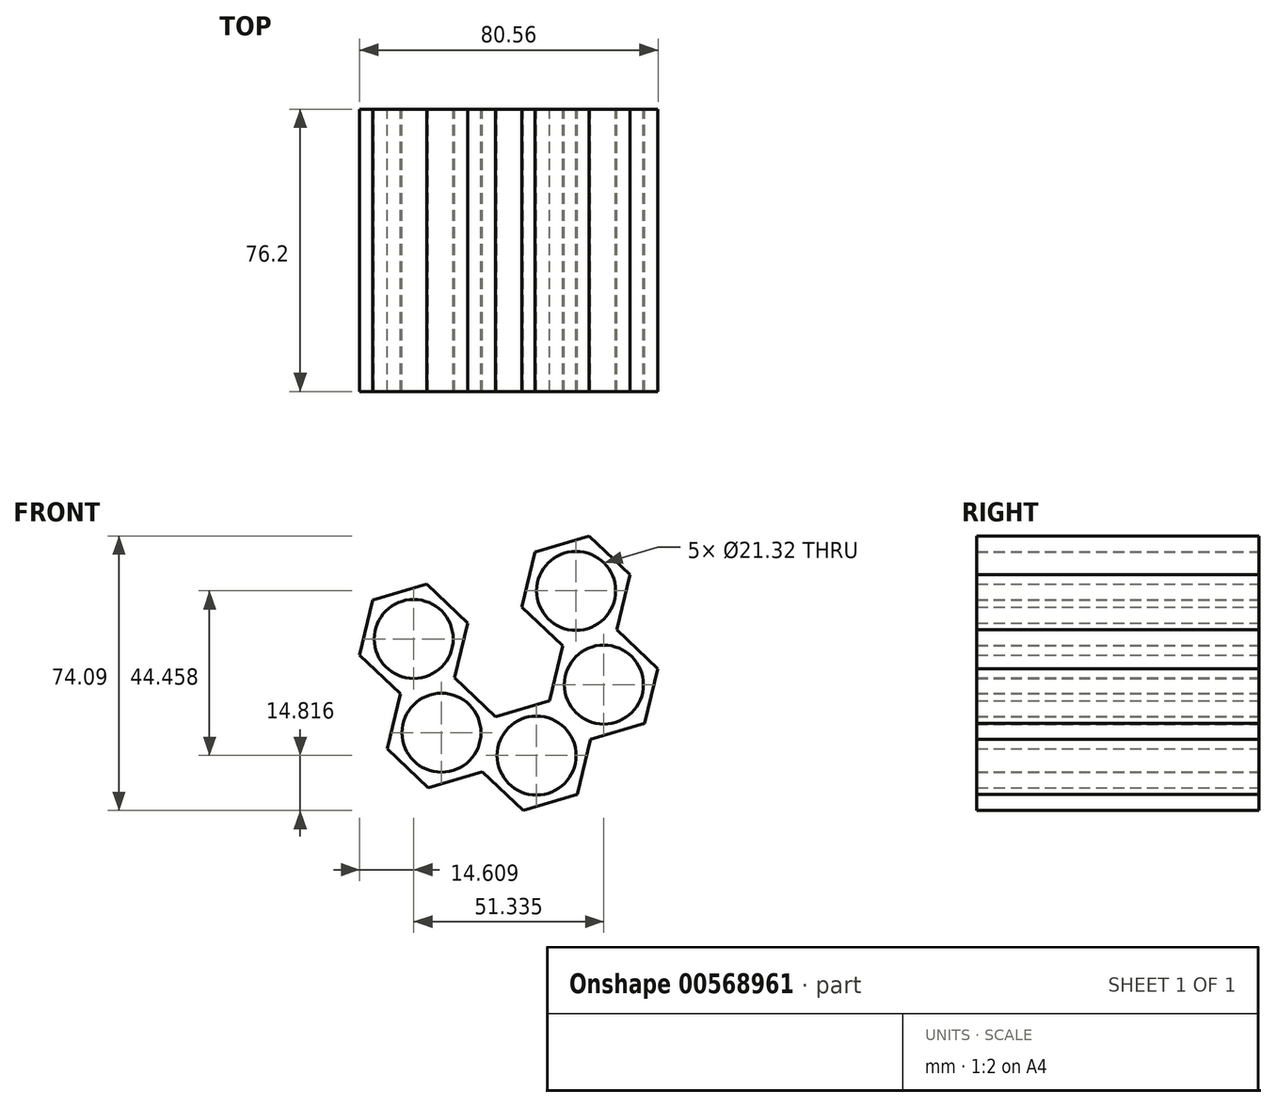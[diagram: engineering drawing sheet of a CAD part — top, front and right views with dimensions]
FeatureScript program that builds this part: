
annotation { "Feature Type Name" : "Feature", "Feature Type Description" : "" }
export const myFeature = defineFeature(function(context is Context, id is Id, definition is map)
    precondition{}
    {
        {
            var Q0;
            Q0=qCreatedBy(makeId("Front.planeOp"),FACE);
            var sketch = newSketch(context, id + "F0", { "sketchPlane" : qUnion([Q0])});
            skCircle(sketch, "E0.cCircle", {"center": v(-51.5, 29.02) * mm, "radius": 13.2 * mm, "construction": true});
            skLineSegment(sketch, "E0.0", {"start": v(-36.89, 33.35) * mm, "end": v(-40.45, 18.53) * mm});
            skLineSegment(sketch, "E0.1", {"start": v(-40.45, 18.53) * mm, "end": v(-55.06, 14.2) * mm});
            skLineSegment(sketch, "E0.2", {"start": v(-55.06, 14.2) * mm, "end": v(-66.11, 24.7) * mm});
            skLineSegment(sketch, "E0.3", {"start": v(-66.11, 24.7) * mm, "end": v(-62.56, 39.51) * mm});
            skLineSegment(sketch, "E0.4", {"start": v(-62.56, 39.51) * mm, "end": v(-47.94, 43.84) * mm});
            skLineSegment(sketch, "E0.5", {"start": v(-47.94, 43.84) * mm, "end": v(-36.89, 33.35) * mm});
            skPoint(sketch, "E0.0.midPoint", {"position": v(-38.67, 25.94) * mm});
            skCircle(sketch, "E1.cCircle", {"center": v(-25.83, 22.86) * mm, "radius": 13.2 * mm, "construction": true});
            skLineSegment(sketch, "E1.0", {"start": v(-11.22, 27.2) * mm, "end": v(-14.78, 12.37) * mm});
            skLineSegment(sketch, "E1.1", {"start": v(-14.78, 12.37) * mm, "end": v(-29.4, 8.05) * mm});
            skLineSegment(sketch, "E1.2", {"start": v(-29.4, 8.05) * mm, "end": v(-40.45, 18.53) * mm});
            skLineSegment(sketch, "E1.3", {"start": v(-40.45, 18.53) * mm, "end": v(-36.89, 33.35) * mm});
            skLineSegment(sketch, "E1.4", {"start": v(-36.89, 33.35) * mm, "end": v(-22.28, 37.68) * mm});
            skLineSegment(sketch, "E1.5", {"start": v(-22.28, 37.68) * mm, "end": v(-11.22, 27.2) * mm});
            skPoint(sketch, "E1.0.midPoint", {"position": v(-13, 19.78) * mm});
            skCircle(sketch, "E2.cCircle", {"center": v(-33.33, 48.17) * mm, "radius": 13.2 * mm, "construction": true});
            skLineSegment(sketch, "E2.0", {"start": v(-18.72, 52.5) * mm, "end": v(-22.28, 37.68) * mm});
            skLineSegment(sketch, "E2.1", {"start": v(-22.28, 37.68) * mm, "end": v(-36.89, 33.35) * mm});
            skLineSegment(sketch, "E2.2", {"start": v(-36.89, 33.35) * mm, "end": v(-47.94, 43.84) * mm});
            skLineSegment(sketch, "E2.3", {"start": v(-47.94, 43.84) * mm, "end": v(-44.39, 58.66) * mm});
            skLineSegment(sketch, "E2.4", {"start": v(-44.39, 58.66) * mm, "end": v(-29.78, 63) * mm});
            skLineSegment(sketch, "E2.5", {"start": v(-29.78, 63) * mm, "end": v(-18.72, 52.5) * mm});
            skPoint(sketch, "E2.0.midPoint", {"position": v(-20.5, 45.1) * mm});
            skCircle(sketch, "E3.cCircle", {"center": v(-7.67, 42.01) * mm, "radius": 13.2 * mm, "construction": true});
            skLineSegment(sketch, "E3.0", {"start": v(6.95, 46.34) * mm, "end": v(3.4, 31.52) * mm});
            skLineSegment(sketch, "E3.1", {"start": v(3.4, 31.52) * mm, "end": v(-11.22, 27.2) * mm});
            skLineSegment(sketch, "E3.2", {"start": v(-11.22, 27.2) * mm, "end": v(-22.28, 37.68) * mm});
            skLineSegment(sketch, "E3.3", {"start": v(-22.28, 37.68) * mm, "end": v(-18.72, 52.5) * mm});
            skLineSegment(sketch, "E3.4", {"start": v(-18.72, 52.5) * mm, "end": v(-4.1, 56.83) * mm});
            skLineSegment(sketch, "E3.5", {"start": v(-4.1, 56.83) * mm, "end": v(6.95, 46.34) * mm});
            skPoint(sketch, "E3.0.midPoint", {"position": v(5.17, 38.93) * mm});
            skCircle(sketch, "E4.cCircle", {"center": v(-44, 3.72) * mm, "radius": 13.2 * mm, "construction": true});
            skLineSegment(sketch, "E4.0", {"start": v(-29.4, 8.05) * mm, "end": v(-32.95, -6.77) * mm});
            skLineSegment(sketch, "E4.1", {"start": v(-32.95, -6.77) * mm, "end": v(-47.56, -11.1) * mm});
            skLineSegment(sketch, "E4.2", {"start": v(-47.56, -11.1) * mm, "end": v(-58.61, -0.61) * mm});
            skLineSegment(sketch, "E4.3", {"start": v(-58.61, -0.61) * mm, "end": v(-55.06, 14.2) * mm});
            skLineSegment(sketch, "E4.4", {"start": v(-55.06, 14.2) * mm, "end": v(-40.45, 18.53) * mm});
            skLineSegment(sketch, "E4.5", {"start": v(-40.45, 18.53) * mm, "end": v(-29.4, 8.05) * mm});
            skPoint(sketch, "E4.0.midPoint", {"position": v(-31.17, 0.64) * mm});
            skCircle(sketch, "E5.cCircle", {"center": v(-0.17, 16.7) * mm, "radius": 13.2 * mm, "construction": true});
            skLineSegment(sketch, "E5.0", {"start": v(10.89, 6.21) * mm, "end": v(-3.72, 1.89) * mm});
            skLineSegment(sketch, "E5.1", {"start": v(-3.72, 1.89) * mm, "end": v(-14.78, 12.37) * mm});
            skLineSegment(sketch, "E5.2", {"start": v(-14.78, 12.37) * mm, "end": v(-11.22, 27.2) * mm});
            skLineSegment(sketch, "E5.3", {"start": v(-11.22, 27.2) * mm, "end": v(3.4, 31.52) * mm});
            skLineSegment(sketch, "E5.4", {"start": v(3.4, 31.52) * mm, "end": v(14.45, 21.03) * mm});
            skLineSegment(sketch, "E5.5", {"start": v(14.45, 21.03) * mm, "end": v(10.89, 6.21) * mm});
            skPoint(sketch, "E5.0.midPoint", {"position": v(3.58, 4.05) * mm});
            skCircle(sketch, "E6.cCircle", {"center": v(-18.33, -2.44) * mm, "radius": 13.2 * mm, "construction": true});
            skLineSegment(sketch, "E6.0", {"start": v(-7.28, -12.93) * mm, "end": v(-21.9, -17.26) * mm});
            skLineSegment(sketch, "E6.1", {"start": v(-21.9, -17.26) * mm, "end": v(-32.95, -6.77) * mm});
            skLineSegment(sketch, "E6.2", {"start": v(-32.95, -6.77) * mm, "end": v(-29.4, 8.05) * mm});
            skLineSegment(sketch, "E6.3", {"start": v(-29.4, 8.05) * mm, "end": v(-14.78, 12.37) * mm});
            skLineSegment(sketch, "E6.4", {"start": v(-14.78, 12.37) * mm, "end": v(-3.72, 1.89) * mm});
            skLineSegment(sketch, "E6.5", {"start": v(-3.72, 1.89) * mm, "end": v(-7.28, -12.93) * mm});
            skPoint(sketch, "E6.0.midPoint", {"position": v(-14.59, -15.1) * mm});
            skCircle(sketch, "E7", {"center": v(-33.33, 48.17) * mm, "radius": 10.66 * mm});
            skCircle(sketch, "E8", {"center": v(-7.67, 42.01) * mm, "radius": 10.66 * mm});
            skCircle(sketch, "E9", {"center": v(-0.17, 16.7) * mm, "radius": 10.66 * mm});
            skCircle(sketch, "E10", {"center": v(-25.83, 22.86) * mm, "radius": 10.66 * mm});
            skCircle(sketch, "E11", {"center": v(-51.5, 29.02) * mm, "radius": 10.66 * mm});
            skCircle(sketch, "E12", {"center": v(-44, 3.72) * mm, "radius": 10.66 * mm});
            skCircle(sketch, "E13", {"center": v(-18.33, -2.44) * mm, "radius": 10.66 * mm});
            skSolve(sketch);
        }
        {
            var Q0;
            Q0=makeQuery(id+"F0.imprint","IMPRINT",FACE,{"disambiguationData":[TD([[makeQuery(id+"F0.imprint","IMPRINT",EDGE,{"derivedFrom":sQuery(id+"F0.wireOp",EDGE,"E2.1")}),-1.0]])]});
            var Q1;
            Q1=makeQuery(id+"F0.imprint","IMPRINT",FACE,{"disambiguationData":[TD([[makeQuery(id+"F0.imprint","IMPRINT",EDGE,{"derivedFrom":sQuery(id+"F0.wireOp",EDGE,"E0.2")}),-1.0]])]});
            var Q2;
            Q2=makeQuery(id+"F0.imprint","IMPRINT",FACE,{"disambiguationData":[TD([[makeQuery(id+"F0.imprint","IMPRINT",EDGE,{"derivedFrom":sQuery(id+"F0.wireOp",EDGE,"E1.3")}),-1.0]])]});
            var Q3;
            Q3=makeQuery(id+"F0.imprint","IMPRINT",FACE,{"disambiguationData":[TD([[makeQuery(id+"F0.imprint","IMPRINT",EDGE,{"derivedFrom":sQuery(id+"F0.wireOp",EDGE,"E4.1")}),-1.0]])]});
            var Q4;
            Q4=makeQuery(id+"F0.imprint","IMPRINT",FACE,{"disambiguationData":[TD([[makeQuery(id+"F0.imprint","IMPRINT",EDGE,{"derivedFrom":sQuery(id+"F0.wireOp",EDGE,"E6.0")}),-1.0]])]});
            var Q5;
            Q5=makeQuery(id+"F0.imprint","IMPRINT",FACE,{"disambiguationData":[TD([[makeQuery(id+"F0.imprint","IMPRINT",EDGE,{"derivedFrom":sQuery(id+"F0.wireOp",EDGE,"E5.0")}),-1.0]])]});
            var Q6;
            Q6=makeQuery(id+"F0.imprint","IMPRINT",FACE,{"disambiguationData":[TD([[makeQuery(id+"F0.imprint","IMPRINT",EDGE,{"derivedFrom":sQuery(id+"F0.wireOp",EDGE,"E3.0")}),-1.0]])]});
            extrude(context, id + "F1", {"entities" : qUnion([Q0, Q1, Q2, Q3, Q4, Q5, Q6]), "depth" : 76.2 * mm, "offsetDistance" : 25.4 * mm});
        }
    });
